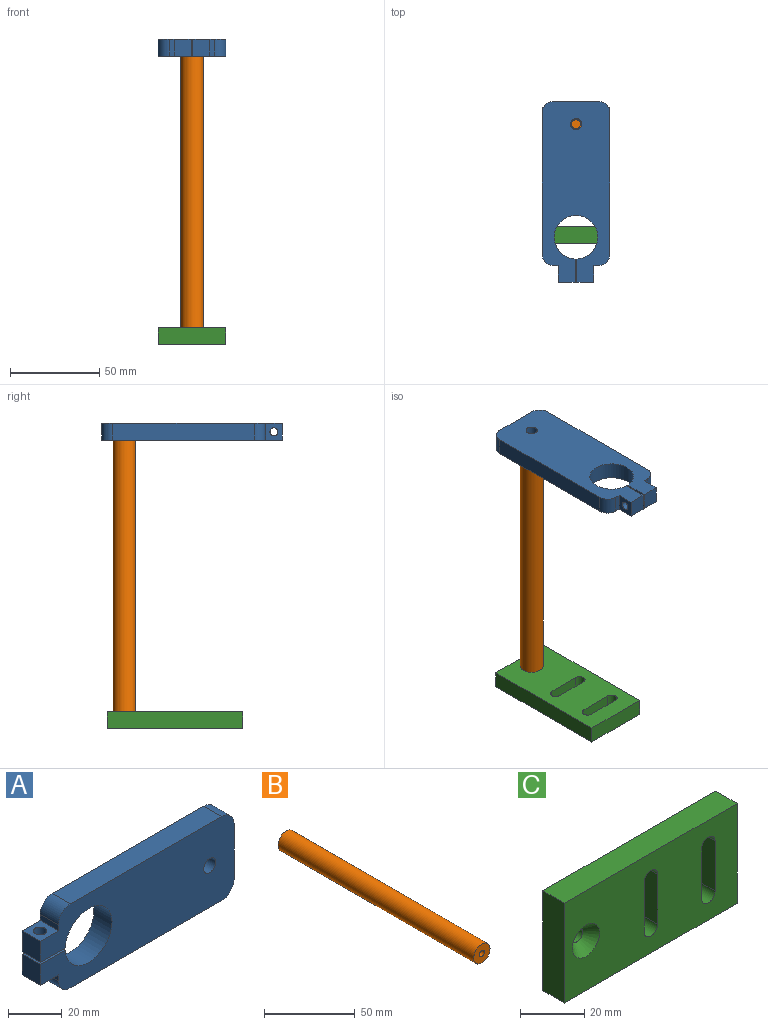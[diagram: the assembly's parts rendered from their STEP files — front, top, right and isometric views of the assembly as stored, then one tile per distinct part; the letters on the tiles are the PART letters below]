
ASSEMBLY  parts=3 mates=3
PART A: 21 faces, bbox 101.6x9.5x38.1 mm
  f0: plane 79.38x9.53mm, normal (0,0,-1), area 756mm2, adj f1,f15,f17,f18
  f1: cylinder r=6.35mm len=9.53mm, axis (0,1,0), area 95mm2, adj f0,f2,f17,f18
  f2: plane 25.4x9.53mm, normal (1,0,0), area 241.9mm2, adj f1,f3,f17,f18
  f3: cylinder r=6.35mm len=9.53mm, axis (0,1,0), area 95mm2, adj f2,f4,f17,f18
  f4: plane 79.38x9.53mm, normal (0,0,1), area 756mm2, adj f3,f5,f17,f18
  f5: cylinder r=6.35mm len=9.53mm, axis (0,1,0), area 95mm2, adj f4,f6,f17,f18
  f6: plane 9.53x2.69mm, normal (-1,0,0), area 25.6mm2, adj f5,f7,f17,f18
  f7: plane 9.53x9.53mm, normal (0,0,1), area 71.1mm2, adj f6,f8,f17,f18,f19
  f8: plane 9.53x9.51mm, normal (-1,0,0), area 90.6mm2, adj f7,f9,f17,f18
  f9: plane 13.15x9.53mm, normal (0,0,-1), area 105.7mm2, adj f8,f10,f17,f18,f19
  f10: cylinder r=12.26mm len=24.51mm, axis (0,1,0), area 724mm2, adj f9,f11,f17,f18
  f11: plane 13.15x9.53mm, normal (0,0,1), area 109.4mm2, adj f10,f12,f17,f18,f20
  f12: plane 9.53x9.51mm, normal (-1,0,0), area 90.6mm2, adj f11,f13,f17,f18
  f13: plane 9.53x9.53mm, normal (0,0,-1), area 74.8mm2, adj f12,f14,f17,f18,f20
  f14: plane 9.53x2.69mm, normal (-1,0,0), area 25.6mm2, adj f13,f15,f17,f18
  f15: cylinder r=6.35mm len=9.53mm, axis (0,1,0), area 95mm2, adj f0,f14,f17,f18
  f16: cylinder r=3.17mm len=9.53mm, axis (0,1,0), area 190mm2, adj f17,f18
  f17: plane 101.6x38.1mm, normal (0,-1,0), area 3147.5mm2, adj f0,f1,f2,f3,f4,f5,f6,f7
  f18: plane 101.6x38.1mm, normal (0,1,0), area 3147.5mm2, adj f0,f1,f2,f3,f4,f5,f6,f7
  f19: cylinder r=2.5mm len=9.51mm, axis (0,0,1), area 149.4mm2, adj f7,f9
  f20: cylinder r=2.25mm len=9.51mm, axis (0,0,-1), area 134.5mm2, adj f11,f13
PART B: 7 faces, bbox 12.7x152.4x12.7 mm
  f0: cylinder r=6.35mm len=152.4mm, axis (0,1,0), area 6080.5mm2, adj f1,f2
  f1: plane 12.7x12.7mm, normal (0,-1,0), area 112.9mm2, adj f0,f5
  f2: plane 12.7x12.7mm, normal (0,1,0), area 106.2mm2, adj f0,f3
  f3: cylinder r=2.55mm len=25.4mm, axis (0,1,0), area 407.4mm2, adj f2,f4
  f4: plane 5.11x5.11mm, normal (0,1,0), area 20.5mm2, adj f3
  f5: cylinder r=2.1mm len=25.4mm, axis (0,-1,0), area 334.4mm2, adj f1,f6
  f6: plane 4.19x4.19mm, normal (0,-1,0), area 13.8mm2, adj f5
PART C: 16 faces, bbox 76.2x9.5x38.1 mm
  f0: plane 76.2x38.1mm, normal (0,-1,0), area 2505.5mm2, adj f2,f3,f4,f5,f7,f8,f9,f10
  f1: plane 76.2x38.1mm, normal (0,1,0), area 2598.7mm2, adj f2,f3,f4,f5,f6,f8,f9,f10
  f2: plane 38.1x9.53mm, normal (-1,0,0), area 362.9mm2, adj f0,f1,f3,f5
  f3: plane 76.2x9.53mm, normal (0,0,-1), area 725.8mm2, adj f0,f1,f2,f4
  f4: plane 38.1x9.53mm, normal (1,0,0), area 362.9mm2, adj f0,f1,f3,f5
  f5: plane 76.2x9.53mm, normal (0,0,1), area 725.8mm2, adj f0,f1,f2,f4
  f6: cylinder r=2.5mm len=5.51mm, axis (0,-1,0), area 86.6mm2, adj f1,f7
  f7: cone r=2.5mm half-angle=41deg, axis (0,-1,0), area 142.1mm2, adj f0,f6
  f8: cylinder r=3mm len=9.53mm, axis (0,-1,0), area 89.7mm2, adj f0,f1,f9,f11
  f9: plane 19.05x9.53mm, normal (1,0,0), area 181.5mm2, adj f0,f1,f8,f10
  f10: cylinder r=3mm len=9.53mm, axis (0,-1,0), area 89.7mm2, adj f0,f1,f9,f11
  f11: plane 19.05x9.53mm, normal (-1,0,0), area 181.5mm2, adj f0,f1,f8,f10
  f12: cylinder r=3mm len=9.53mm, axis (0,-1,0), area 89.7mm2, adj f0,f1,f13,f15
  f13: plane 19.05x9.53mm, normal (1,0,0), area 181.5mm2, adj f0,f1,f12,f14
  f14: cylinder r=3mm len=9.53mm, axis (0,-1,0), area 89.7mm2, adj f0,f1,f13,f15
  f15: plane 19.05x9.53mm, normal (-1,0,0), area 181.5mm2, adj f0,f1,f12,f14
PLACE A rot(axis=(0.58,0.58,0.58),120deg) t=(-38.1,3.17,171.45)mm
PLACE B rot(axis=(0,0.71,0.71),180deg) t=(-19.05,-9.52,161.93)mm
PLACE C rot(axis=(0.58,-0.58,-0.58),120deg) t=(0,0,9.52)mm
MATE fastened C.f6 <-> B.f5  axis (0,0,1) through (-19.05,-9.52,9.52)mm
MATE parallel A.f4 <-> C.f3  axis (1,0,0) through (0,-42.86,161.93)mm
MATE revolute B.f3 <-> A.f16  axis (0,0,1) through (-19.05,-9.52,161.93)mm
